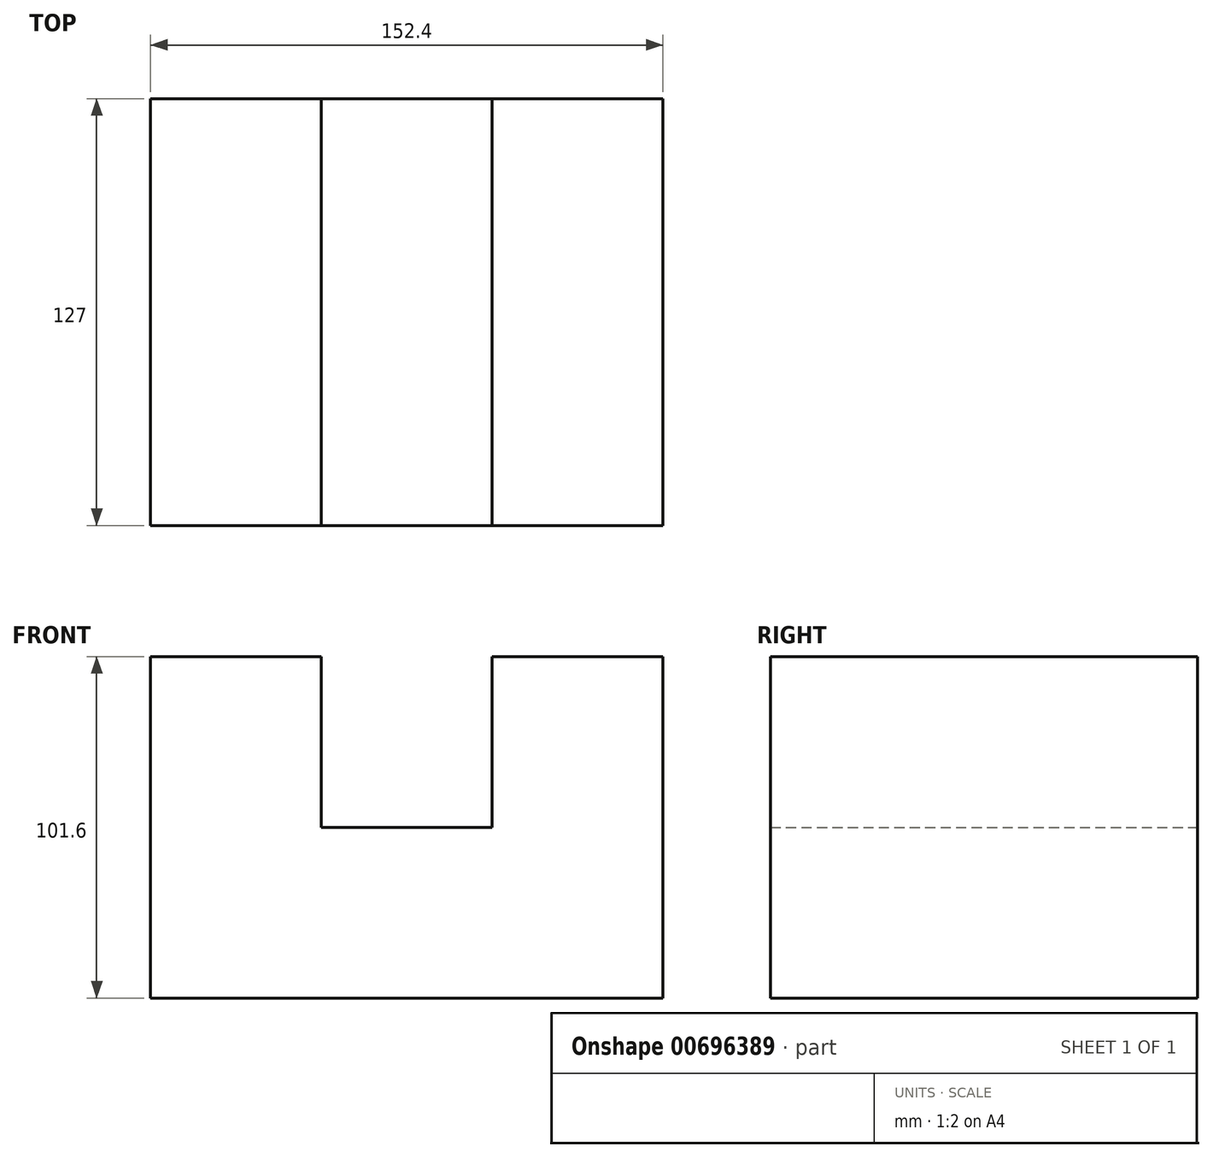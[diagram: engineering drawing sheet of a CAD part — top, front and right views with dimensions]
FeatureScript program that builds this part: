
annotation { "Feature Type Name" : "Feature", "Feature Type Description" : "" }
export const myFeature = defineFeature(function(context is Context, id is Id, definition is map)
    precondition{}
    {
        {
            var Q0;
            Q0=qCreatedBy(makeId("Front.planeOp"),FACE);
            var sketch = newSketch(context, id + "F0", { "sketchPlane" : qUnion([Q0])});
            skLineSegment(sketch, "E0", {"start": v(-76.2, 0) * mm, "end": v(76.2, 0) * mm});
            skLineSegment(sketch, "E1", {"start": v(-76.2, 0) * mm, "end": v(-76.2, 101.6) * mm});
            skLineSegment(sketch, "E2", {"start": v(-76.2, 101.6) * mm, "end": v(-25.4, 101.6) * mm});
            skLineSegment(sketch, "E3", {"start": v(-25.4, 101.6) * mm, "end": v(-25.4, 50.8) * mm});
            skLineSegment(sketch, "E4", {"start": v(-25.4, 50.8) * mm, "end": v(25.4, 50.8) * mm});
            skLineSegment(sketch, "E5", {"start": v(25.4, 50.8) * mm, "end": v(25.4, 101.6) * mm});
            skLineSegment(sketch, "E6", {"start": v(25.4, 101.6) * mm, "end": v(76.2, 101.6) * mm});
            skLineSegment(sketch, "E7", {"start": v(76.2, 101.6) * mm, "end": v(76.2, 0) * mm});
            skSolve(sketch);
        }
        {
            var Q0;
            Q0=makeQuery(id+"F0.imprint","IMPRINT",FACE,{"disambiguationData":[TD([[makeQuery(id+"F0.imprint","IMPRINT",EDGE,{"derivedFrom":sQuery(id+"F0.wireOp",EDGE,"E0")}),1.0]])]});
            extrude(context, id + "F1", {"entities" : qUnion([Q0]), "depth" : 127 * mm, "offsetDistance" : 25.4 * mm});
        }
    });
